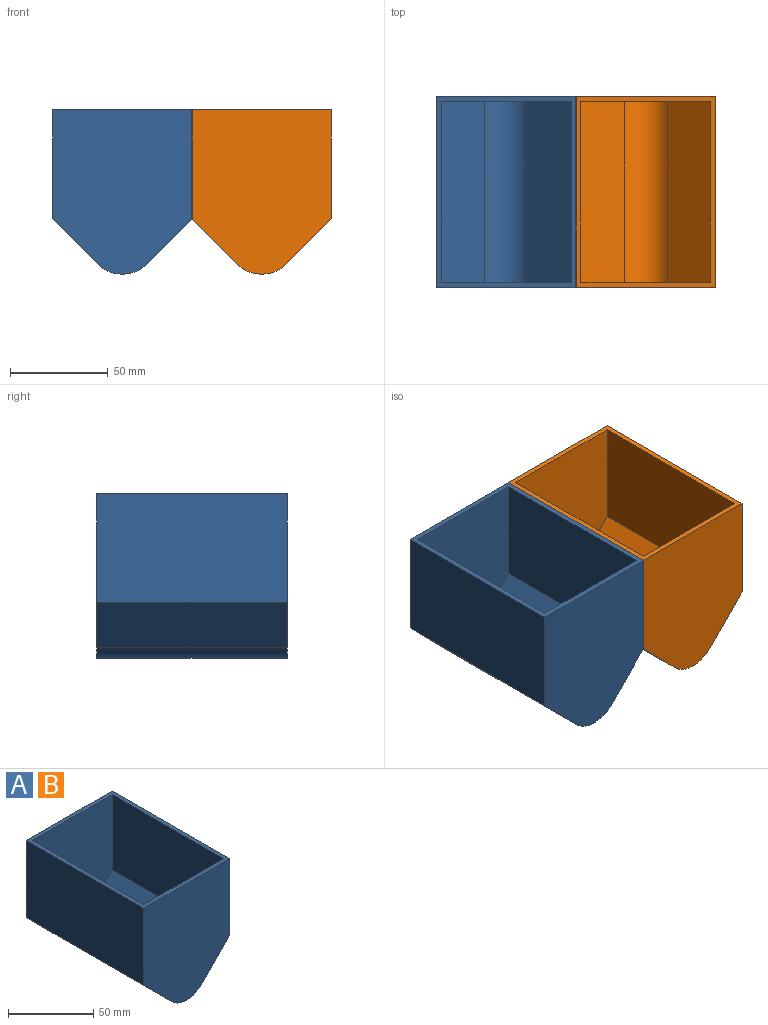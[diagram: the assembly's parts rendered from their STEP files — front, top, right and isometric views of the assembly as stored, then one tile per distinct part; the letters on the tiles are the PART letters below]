
ASSEMBLY  parts=2 mates=1
PART A: 15 faces, bbox 71.3x97.5x84 mm
  f0: plane 97.54x71.27mm, normal (0,0,1), area 831.7mm2, adj f1,f4,f5,f6,f8,f11,f12,f13
  f1: plane 97.54x55.4mm, normal (-1,0,0), area 5403.2mm2, adj f0,f2,f5,f6
  f2: plane 97.54x23.24mm, normal (-0.71,0,-0.7), area 3180.4mm2, adj f1,f5,f6,f7
  f3: plane 97.54x23.24mm, normal (0.71,0,-0.7), area 3180.4mm2, adj f4,f5,f6,f7
  f4: plane 97.54x55.4mm, normal (1,0,0), area 5403.2mm2, adj f0,f3,f5,f6
  f5: plane 83.98x71.27mm, normal (0,-1,0), area 5167.1mm2, adj f0,f1,f2,f3,f4,f7
  f6: plane 83.98x71.27mm, normal (0,1,0), area 5167.1mm2, adj f0,f1,f2,f3,f4,f7
  f7: cylinder r=17.91mm len=97.54mm, axis (0,1,0), area 2771.2mm2, adj f2,f3,f5,f6
  f8: plane 92.46x54.36mm, normal (1,0,0), area 5025.6mm2, adj f0,f9,f12,f13
  f9: plane 92.46x22.5mm, normal (0.71,0,0.7), area 2918.5mm2, adj f8,f12,f13,f14
  f10: plane 92.46x22.5mm, normal (-0.71,0,0.7), area 2918.5mm2, adj f11,f12,f13,f14
  f11: plane 92.46x54.36mm, normal (-1,0,0), area 5025.6mm2, adj f0,f10,f12,f13
  f12: plane 81.44x66.19mm, normal (0,1,0), area 4658.2mm2, adj f0,f8,f9,f10,f11,f14
  f13: plane 81.44x66.19mm, normal (0,-1,0), area 4658.2mm2, adj f0,f8,f9,f10,f11,f14
  f14: cylinder r=15.37mm len=92.46mm, axis (0,1,0), area 2254.3mm2, adj f9,f10,f12,f13
PART B: same geometry as A
PLACE A t=(-51.75,35.5,-39.23)mm
PLACE B t=(19.52,35.5,-39.23)mm
MATE fastened A.f4 <-> B.f1  axis (1,0,0) through (-86.65,-13.27,2.9)mm
